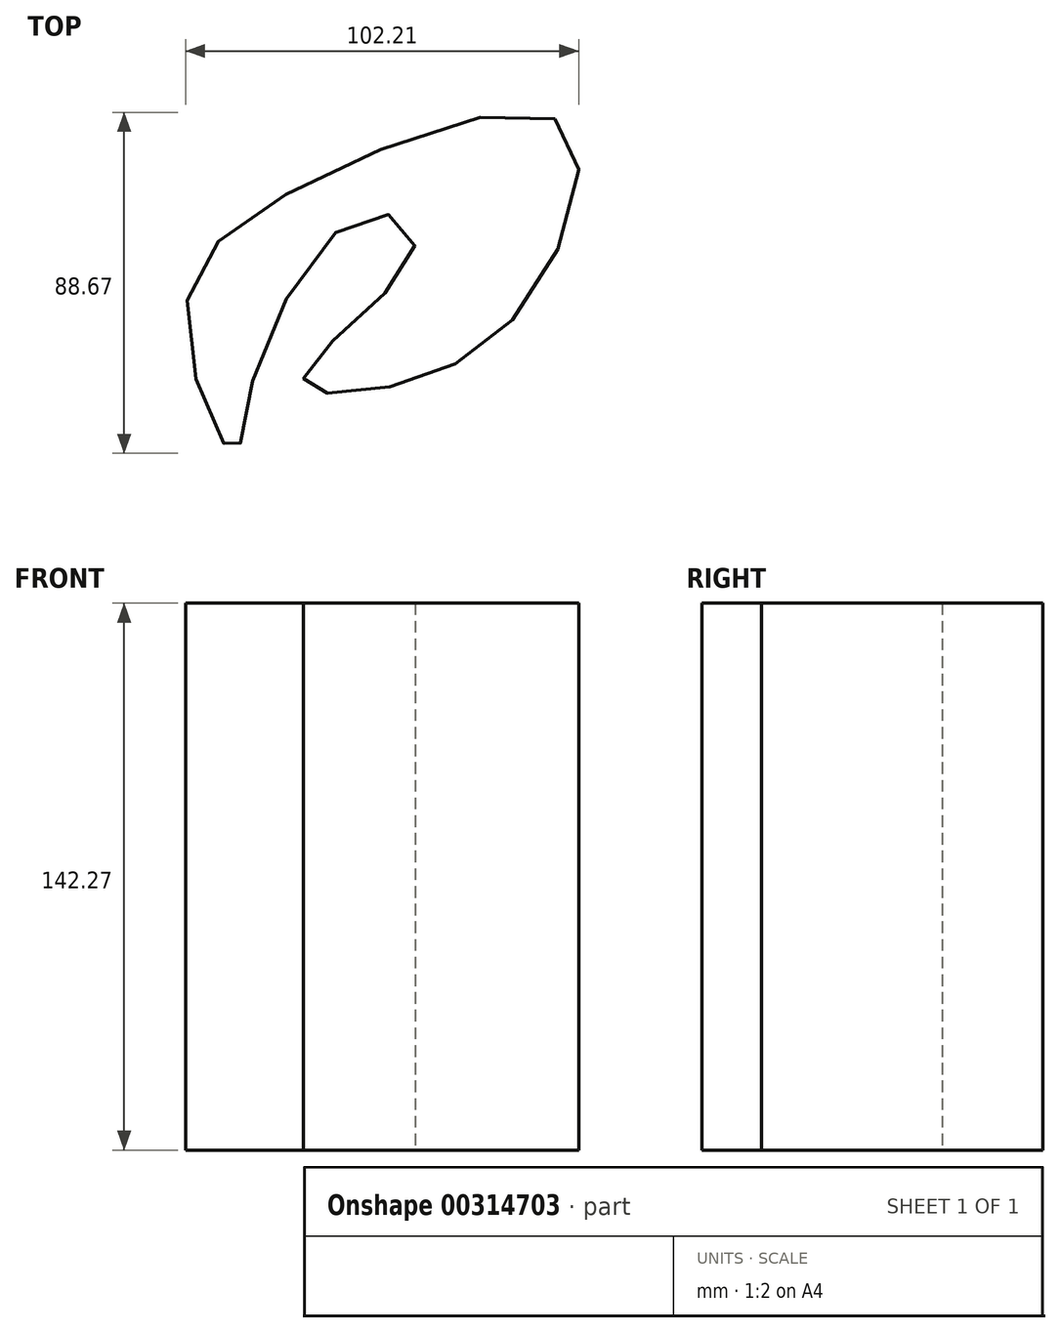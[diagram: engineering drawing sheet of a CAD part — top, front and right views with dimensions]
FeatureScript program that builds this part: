
annotation { "Feature Type Name" : "Feature", "Feature Type Description" : "" }
export const myFeature = defineFeature(function(context is Context, id is Id, definition is map)
    precondition{}
    {
        {
            var Q0;
            Q0=qCreatedBy(makeId("Top.planeOp"),FACE);
            var sketch = newSketch(context, id + "F0", { "sketchPlane" : qUnion([Q0])});
            skFitSpline(sketch, "E0", {"points": [v(7.28, 11.69) * mm, v(0, 0) * mm, v(22.87, 0) * mm, v(59.12, 23.71) * mm, v(67.42, 67.92) * mm, v(0, 52.51) * mm, v(-31, 18.3) * mm, v(-18.63, -17.45) * mm, v(-13.89, 0) * mm, v(15.75, 44.55) * mm, v(28.63, 37.27) * mm, v(7.28, 11.69) * mm]});
            skSolve(sketch);
        }
        {
            var Q0;
            Q0=makeQuery(id+"F0.imprint","IMPRINT",FACE,{"disambiguationData":[TD([[makeQuery(id+"F0.imprint","IMPRINT",EDGE,{"derivedFrom":sQuery(id+"F0.wireOp",EDGE,"E0")}),1.0]])]});
            extrude(context, id + "F1", {"entities" : qUnion([Q0]), "depth" : 142.27 * mm});
        }
    });
